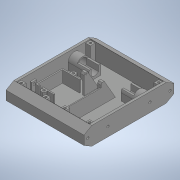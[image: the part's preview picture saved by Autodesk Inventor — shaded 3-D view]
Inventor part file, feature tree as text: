
AUTODESK INVENTOR PART (.ipt)
format: ipt  version: 2020 (Build 240168000, 168)  size: 607,744 bytes
history: native  units: in
note: dims shown in document units (in); Inventor stores cm internally (conversion verified against a paired STEP export)
features: extrude x18, sketch x17, projected_geometry x14, mirror x6, plane x1
ambient origin geometry x8: Origin, YZ Plane, XZ Plane, XY Plane, X Axis, Y Axis, Z Axis, Center Point
bodies: Solid1 (feature_tree)
feature tree (56):
  extrude  "Extrusion1"  Depth=5.9055in
  extrude  "Extrusion2"  TaperAngle=0.0deg  [1 undecoded]
  extrude  "Extrusion3"  Depth=1.063in
  extrude  "Extrusion4"  Depth=0.315in
  extrude  "Extrusion5"  TaperAngle=0.0deg  [1 undecoded]
  extrude  "Extrusion6"  Depth=0.5906in
  mirror  "Mirror1"
  extrude  "Extrusion7"  Depth=0.0787in
  mirror  "Mirror2"
  extrude  "Extrusion8"  Depth=0.6102in
  mirror  "Mirror3"
  plane  "Work Plane1"
  extrude  "Extrusion9"  Depth=0.7874in TaperAngle=0.0deg
  mirror  "Mirror4"
  extrude  "Extrusion10"  Depth=6.063in TaperAngle=0.0deg
  extrude  "Extrusion11"  Depth=0.1575in
  extrude  "Extrusion12"  TaperAngle=0.0deg  [1 undecoded]
  extrude  "Extrusion13"  Depth=0.2756in
  extrude  "Extrusion14"  Depth=0.4331in
  extrude  "Extrusion17"  Depth=2.7559in
  extrude  "Extrusion18"  Depth=0.0413in
  mirror  "Mirror6"
  extrude  "Extrusion19"  TaperAngle=0.0deg  [1 undecoded]
  mirror  "Mirror7"
  extrude  "Extrusion20"  TaperAngle=60.0deg  [1 undecoded]
  sketch  "Sketch1"  dims[d0=1.1811in d1=5.9055in]
  sketch  "Sketch2"  dims[d2=5.1181in d3=0.0in]
  projected_geometry  "Projected Loop1"
  sketch  "Sketch3"  dims[d4=0.1575in d5=1.063in]
  projected_geometry  "Projected Loop2"
  projected_geometry  "Projected Loop3"
  sketch  "Sketch4"  dims[d6=0.0in d8=0.315in]
  projected_geometry  "Projected Loop4"
  sketch  "Sketch6"  dims[d10=0.993in d11=0.0in]
  sketch  "Sketch7"  dims[d12=0.6496in d13=0.5906in]
  sketch  "Sketch9"  dims[d14=1.5748in d15=0.0787in]
  sketch  "Sketch10"  dims[d16=0.5512in d17=0.0in d18=0.6102in]
  sketch  "Sketch12"  dims[d19=0.4803in d20=0.7874in d21=0.0in]
  projected_geometry  "Projected Loop6"
  projected_geometry  "Projected Loop7"
  projected_geometry  "Projected Loop8"
  sketch  "Sketch13"  dims[d22=0.1654in d23=6.063in d24=0.0in]
  sketch  "Sketch14"  dims[d25=0.5114in d26=0.1575in]
  sketch  "Sketch15"  dims[d27=1.5748in d28=0.0in d29=0.0in]
  projected_geometry  "Projected Loop15"
  sketch  "Sketch16"  dims[d30=0.1575in d31=0.2756in]
  projected_geometry  "Projected Loop19"
  projected_geometry  "Projected Loop20"
  projected_geometry  "Projected Loop21"
  projected_geometry  "Projected Loop22"
  projected_geometry  "Projected Loop23"
  projected_geometry  "Projected Loop24"
  sketch  "Sketch20"  dims[d32=0.0in d33=0.4331in]
  sketch  "Sketch21"  dims[d34=0.0827in d38=2.7559in]
  sketch  "Sketch22"  dims[d40=0.0413in d41=0.0909in]
  sketch  "Sketch23"  dims[d42=0.2362in d43=0.0in d44=60.0deg d45=0.0787in d46=0.315in d48=0.993in d49=0.0in d53=0.2756in d54=0.0in d55=0.4724in d56=1.2008in d57=1.6142in d58=1.5945in d59=0.0787in d60=0.0787in d62=0.315in d63=0.7677in d64=0.0in d66=0.1476in d67=0.2756in d68=0.0in d69=0.7874in d70=0.2953in d71=0.1181in d72=0.0in d89=0.0157in d90=0.0157in d91=0.1476in d92=0.1476in d96=0.315in d97=0.1575in d98=0.1181in d99=0.0in d102=0.1772in d104=0.3346in d105=135.0deg d106=0.2362in d107=0.0in d108=0.0394in d109=0.0in d110=0.063in d111=0.0394in d112=0.0in]
note: 5 required parameter values undecoded (feature->parameter linkage not recoverable at this tier; creation-order binding heuristic only, values carry confidence <= 0.55)
